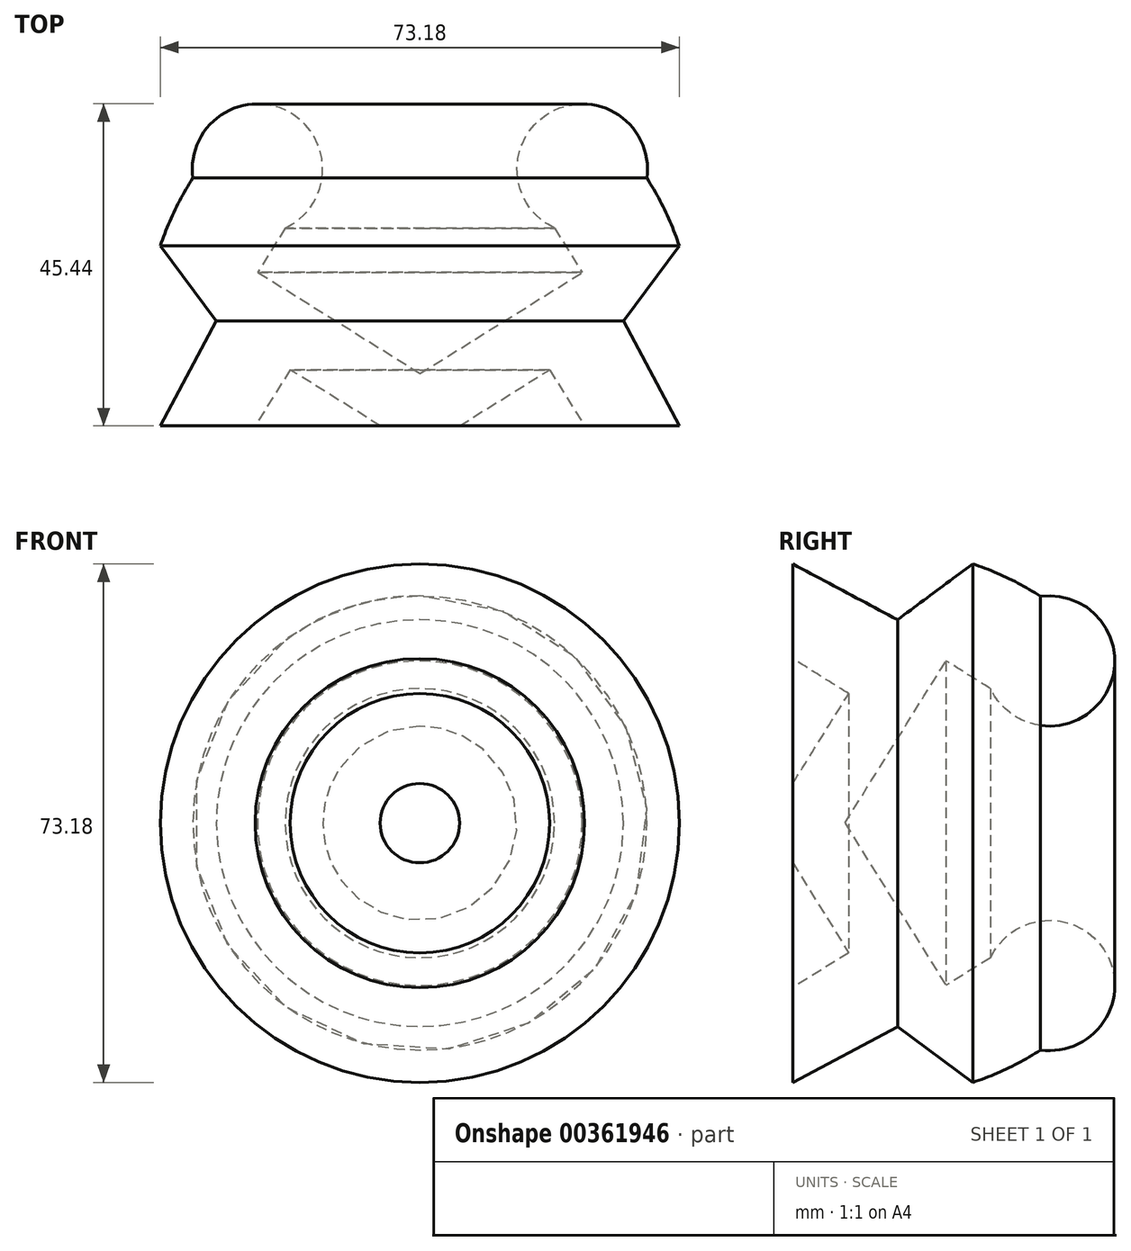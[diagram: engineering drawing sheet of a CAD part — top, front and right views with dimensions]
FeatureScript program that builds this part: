
annotation { "Feature Type Name" : "Feature", "Feature Type Description" : "" }
export const myFeature = defineFeature(function(context is Context, id is Id, definition is map)
    precondition{}
    {
        {
            var Q0;
            Q0=qCreatedBy(makeId("Top.planeOp"),FACE);
            var sketch = newSketch(context, id + "F0", { "sketchPlane" : qUnion([Q0])});
            skArc(sketch, "E0", {"start": v(-32.02, 20.17) * mm, "mid": v(-34.62, 15.54) * mm, "end": v(-36.6, 10.6) * mm});
            skLineSegment(sketch, "E1", {"start": v(0, -7.43) * mm, "end": v(0, -14.8) * mm});
            skPoint(sketch, "E2.orphan", {"position": v(0, 38.71) * mm});
            skLineSegment(sketch, "E3", {"start": v(-36.6, -14.8) * mm, "end": v(-23.23, -14.8) * mm});
            skPoint(sketch, "E4.orphan", {"position": v(0, -42.9) * mm});
            skArc(sketch, "E5", {"start": v(-19, 13.12) * mm, "mid": v(-18.53, 29.54) * mm, "end": v(-32.02, 20.17) * mm});
            skLineSegment(sketch, "E6", {"start": v(-19, 13.12) * mm, "end": v(-22.9, 6.84) * mm});
            skLineSegment(sketch, "E7", {"start": v(-22.9, 6.84) * mm, "end": v(0, -7.43) * mm});
            skPoint(sketch, "E8.orphan", {"position": v(0, 20.17) * mm});
            skLineSegment(sketch, "E9", {"start": v(-36.6, 10.6) * mm, "end": v(-28.71, 0) * mm});
            skLineSegment(sketch, "E10", {"start": v(-28.71, 0) * mm, "end": v(-36.6, -14.8) * mm});
            skLineSegment(sketch, "E11", {"start": v(-23.23, -14.8) * mm, "end": v(-18.3, -6.88) * mm});
            skPoint(sketch, "E11.endSnap0", {"position": v(-18.3, -14.8) * mm});
            skLineSegment(sketch, "E12", {"start": v(-18.3, -6.88) * mm, "end": v(-5.6, -14.8) * mm});
            skLineSegment(sketch, "E13.trimOffspring", {"start": v(-5.6, -14.8) * mm, "end": v(0, -14.8) * mm});
            skSolve(sketch);
        }
        {
            var Q0;
            Q0 = qSketchRegion(id + "F0", true);
            var Q1;
            Q1=sQuery(id+"F0.wireOp",EDGE,"E1");
            revolve(context, id + "F1", {"entities" : qUnion([Q0]), "axis" : qUnion([Q1]), "revolveType" : RevolveType.FULL});
        }
    });
